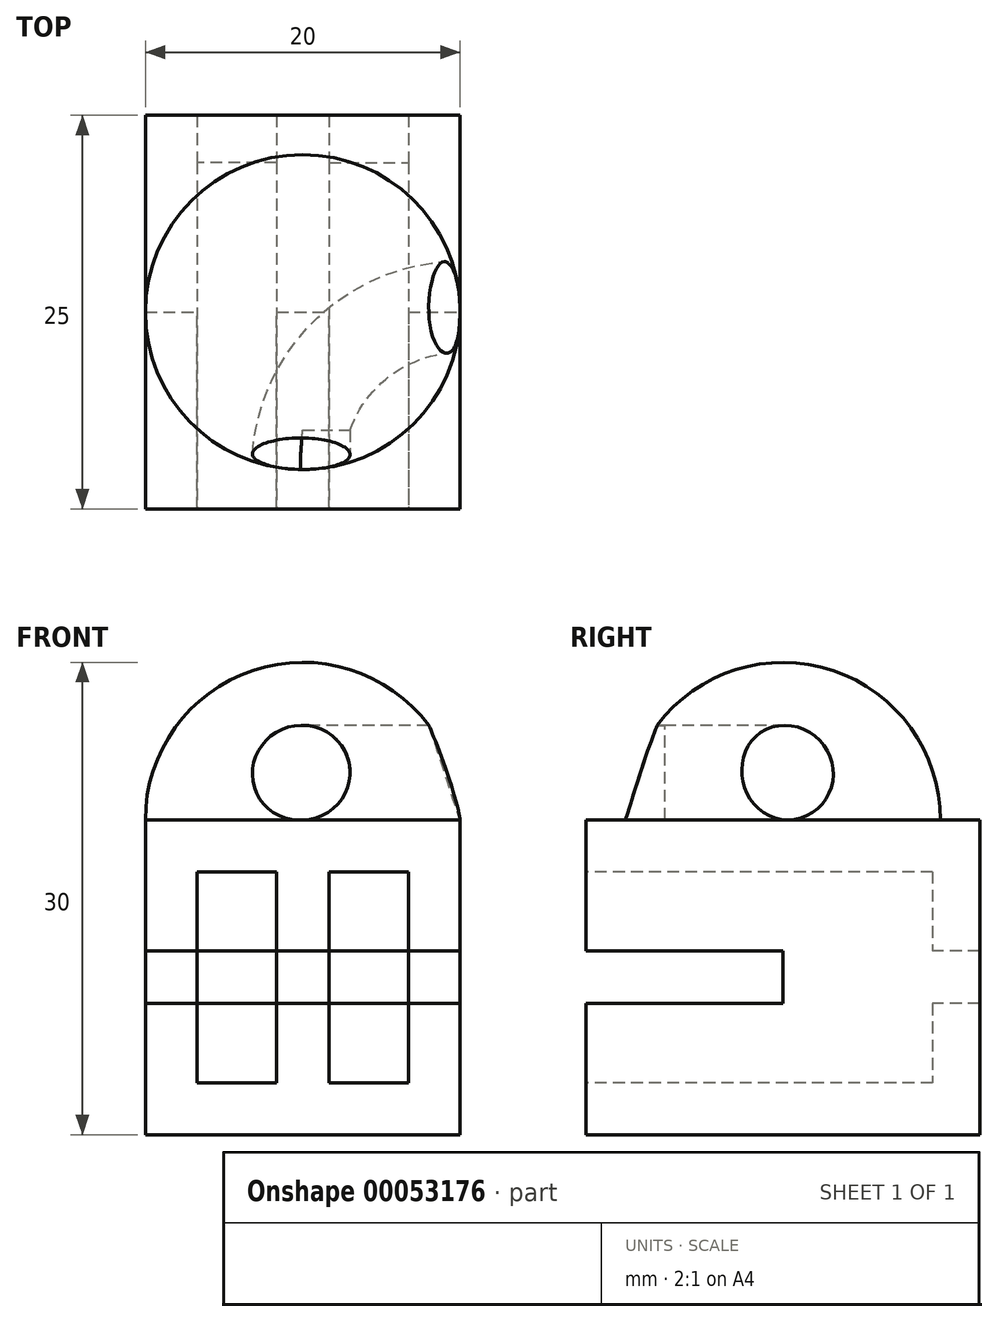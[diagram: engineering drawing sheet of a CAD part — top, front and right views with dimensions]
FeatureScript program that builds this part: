
annotation { "Feature Type Name" : "Feature", "Feature Type Description" : "" }
export const myFeature = defineFeature(function(context is Context, id is Id, definition is map)
    precondition{}
    {
        {
            var Q0;
            Q0=qCreatedBy(makeId("Front.planeOp"),FACE);
            var sketch = newSketch(context, id + "F0", { "sketchPlane" : qUnion([Q0])});
            skLineSegment(sketch, "E0.bottom", {"start": v(0, 0) * mm, "end": v(20, 0) * mm});
            skLineSegment(sketch, "E0.top", {"start": v(0, 20) * mm, "end": v(20, 20) * mm});
            skLineSegment(sketch, "E0.left", {"start": v(0, 0) * mm, "end": v(0, 20) * mm});
            skLineSegment(sketch, "E0.right", {"start": v(20, 0) * mm, "end": v(20, 20) * mm});
            skSolve(sketch);
        }
        {
            var Q0;
            Q0=makeQuery(id+"F0.imprint","IMPRINT",FACE,{"disambiguationData":[TD([[makeQuery(id+"F0.imprint","IMPRINT",EDGE,{"derivedFrom":sQuery(id+"F0.wireOp",EDGE,"E0.bottom")}),1.0]])]});
            extrude(context, id + "F1", {"entities" : qUnion([Q0]), "depth" : 25 * mm});
        }
        {
            var Q0;
            Q0=makeQuery(id+"F1.opExtrude","CAP_FACE",FACE,{"disambiguationData":[OSD([sQuery(id+"F0.wireOp",EDGE,"E0.bottom"),sQuery(id+"F0.wireOp",EDGE,"E0.top"),sQuery(id+"F0.wireOp",EDGE,"E0.left"),sQuery(id+"F0.wireOp",EDGE,"E0.right")])],"isStart":false});
            var sketch = newSketch(context, id + "F2", { "sketchPlane" : qUnion([Q0])});
            skLineSegment(sketch, "E1.rect.bottom", {"start": v(3.3, 16.7) * mm, "end": v(16.7, 16.7) * mm});
            skLineSegment(sketch, "E1.rect.top", {"start": v(3.3, 3.3) * mm, "end": v(16.7, 3.3) * mm});
            skLineSegment(sketch, "E1.rect.left", {"start": v(3.3, 16.7) * mm, "end": v(3.3, 3.3) * mm});
            skLineSegment(sketch, "E1.rect.right", {"start": v(16.7, 16.7) * mm, "end": v(16.7, 3.3) * mm});
            skPoint(sketch, "E1.rect.middle", {"position": v(10, 10) * mm});
            skPoint(sketch, "E1.rect.middle.positionSnap0", {"position": v(10, 20) * mm});
            skPoint(sketch, "E1.rect.middle.positionSnap1", {"position": v(0, 10) * mm});
            skPoint(sketch, "E1.rect.centerSnap0", {"position": v(10, 20) * mm});
            skPoint(sketch, "E1.rect.centerSnap1", {"position": v(0, 10) * mm});
            skSolve(sketch);
        }
        {
            var Q0;
            Q0=makeQuery(id+"F2.imprint","IMPRINT",FACE,{"disambiguationData":[TD([[makeQuery(id+"F2.imprint","IMPRINT",EDGE,{"derivedFrom":sQuery(id+"F2.wireOp",EDGE,"E1.rect.bottom")}),-1.0]])]});
            extrude(context, id + "F3", {"entities" : qUnion([Q0]), "operationType" : NewBodyOperationType.REMOVE, "oppositeDirection" : true, "depth" : 22 * mm});
        }
        {
            var Q0;
            Q0=makeQuery(id+"F1.opExtrude","CAP_FACE",FACE,{"disambiguationData":[OSD([sQuery(id+"F0.wireOp",EDGE,"E0.bottom"),sQuery(id+"F0.wireOp",EDGE,"E0.top"),sQuery(id+"F0.wireOp",EDGE,"E0.left"),sQuery(id+"F0.wireOp",EDGE,"E0.right")])],"isStart":false});
            var sketch = newSketch(context, id + "F4", { "sketchPlane" : qUnion([Q0])});
            skLineSegment(sketch, "E2", {"start": v(11.67, 16.7) * mm, "end": v(11.67, 3.3) * mm});
            skLineSegment(sketch, "E3", {"start": v(8.33, 3.3) * mm, "end": v(8.33, 16.7) * mm});
            skSolve(sketch);
        }
        {
            var Q0;
            {var subQ0=sQuery(id+"F4.wireOp",EDGE,"E2");Q0=makeQuery(id+"F4.imprint","IMPRINT",FACE,{"disambiguationData":[TD([[makeQuery(id+"F4.imprint","IMPRINT",EDGE,{"derivedFrom":subQ0}),-1.0]])]});}
            extrude(context, id + "F5", {"entities" : qUnion([Q0]), "operationType" : NewBodyOperationType.ADD, "oppositeDirection" : true, "depth" : 25 * mm});
        }
        {
            var Q0;
            Q0=makeQuery(id+"F1.opExtrude","SWEPT_FACE",FACE,{"disambiguationData":[OSD([sQuery(id+"F0.wireOp",EDGE,"E0.right")])]});
            var sketch = newSketch(context, id + "F6", { "sketchPlane" : qUnion([Q0])});
            skLineSegment(sketch, "E4", {"start": v(-25, 10) * mm, "end": v(-12.5, 10) * mm});
            skLineSegment(sketch, "E5", {"start": v(-12.5, 11.67) * mm, "end": v(-25, 11.67) * mm});
            skLineSegment(sketch, "E6", {"start": v(-25, 8.33) * mm, "end": v(-12.5, 8.33) * mm});
            skLineSegment(sketch, "E7", {"start": v(-12.5, 11.67) * mm, "end": v(-12.5, 8.33) * mm});
            skSolve(sketch);
        }
        {
            var Q0;
            {var subQ0=sQuery(id+"F6.wireOp",EDGE,"E4");Q0=makeQuery(id+"F6.imprint","IMPRINT",FACE,{"disambiguationData":[TD([[makeQuery(id+"F6.imprint","IMPRINT",EDGE,{"derivedFrom":subQ0}),1.0]])]});}
            var Q1;
            {var subQ0=sQuery(id+"F6.wireOp",EDGE,"E4");Q1=makeQuery(id+"F6.imprint","IMPRINT",FACE,{"disambiguationData":[TD([[makeQuery(id+"F6.imprint","IMPRINT",EDGE,{"derivedFrom":subQ0}),-1.0]])]});}
            extrude(context, id + "F7", {"entities" : qUnion([Q0, Q1]), "operationType" : NewBodyOperationType.REMOVE, "oppositeDirection" : true, "depth" : 25 * mm});
        }
        {
            var Q0;
            Q0=makeQuery(id+"F1.opExtrude","SWEPT_FACE",FACE,{"disambiguationData":[OSD([sQuery(id+"F0.wireOp",EDGE,"E0.top")])]});
            var sketch = newSketch(context, id + "F8", { "sketchPlane" : qUnion([Q0])});
            skLineSegment(sketch, "E8", {"start": v(0, -12.5) * mm, "end": v(10, -12.5) * mm});
            skPoint(sketch, "E8.endSnap0", {"position": v(10, 0) * mm});
            skCircle(sketch, "E9", {"center": v(10, -12.5) * mm, "radius": 10 * mm});
            skLineSegment(sketch, "E10", {"start": v(10, -12.5) * mm, "end": v(10, -2.5) * mm});
            skLineSegment(sketch, "E11", {"start": v(10, -12.5) * mm, "end": v(10, -22.5) * mm});
            skLineSegment(sketch, "E12", {"start": v(10, -22.5) * mm, "end": v(20, -22.5) * mm});
            skSolve(sketch);
        }
        {
            var Q0;
            {var subQ0=sQuery(id+"F8.wireOp",EDGE,"E10");Q0=makeQuery(id+"F8.imprint","IMPRINT",FACE,{"disambiguationData":[TD([[makeQuery(id+"F8.imprint","IMPRINT",EDGE,{"derivedFrom":subQ0}),-1.0]])]});}
            var Q1;
            Q1=sQuery(id+"F8.wireOp",EDGE,"E10");
            revolve(context, id + "F9", {"operationType" : NewBodyOperationType.ADD, "entities" : qUnion([Q0]), "axis" : qUnion([Q1]), "revolveType" : RevolveType.ONE_DIRECTION, "oppositeDirection" : true, "angle" : 180 * degree});
        }
        {
            var Q0;
            Q0=makeQuery(id+"F1.opExtrude","SWEPT_FACE",FACE,{"disambiguationData":[OSD([sQuery(id+"F0.wireOp",EDGE,"E0.right")])]});
            var sketch = newSketch(context, id + "F10", { "sketchPlane" : qUnion([Q0])});
            skLineSegment(sketch, "E13", {"start": v(-22.5, 20) * mm, "end": v(-22.5, 26) * mm});
            skSolve(sketch);
        }
        {
            var Q0;
            Q0=sQuery(id+"F8.wireOp",EDGE,"E12");
            var Q1;
            Q1=sQuery(id+"F10.wireOp",EDGE,"E13");
            cPlane(context, id + "F11", {"entities" : qUnion([Q0, Q1]), "cplaneType" : CPlaneType.LINE_ANGLE, "offset" : 150 * mm, "angle" : 0 * degree, "width" : 150 * mm, "height" : 150 * mm});
        }
        {
            var Q0;
            {var subQ0=sQuery(id+"F2.wireOp",EDGE,"E1.rect.bottom");var subQ1=sQuery(id+"F0.wireOp",EDGE,"E0.right");var subQ2=sQuery(id+"F0.wireOp",EDGE,"E0.left");var subQ3=sQuery(id+"F0.wireOp",EDGE,"E0.top");var subQ4=sQuery(id+"F4.wireOp",EDGE,"E2");var subQ5=sQuery(id+"F4.wireOp",EDGE,"E3");Q0=makeQuery(id+"F7.boolean.opBoolean","SPLIT",FACE,{"disambiguationData":[TD([makeQuery(id+"F1.opExtrude","SWEPT_FACE",FACE,{"disambiguationData":[OSD([subQ3])]})])],"derivedFrom":makeQuery(id+"F5.boolean.opBoolean","MERGE",FACE,{"derivedFrom":[makeQuery(id+"F1.opExtrude","CAP_FACE",FACE,{"disambiguationData":[OSD([sQuery(id+"F0.wireOp",EDGE,"E0.bottom"),subQ3,subQ2,subQ1])],"isStart":false}),makeQuery(id+"F5.opExtrude","CAP_FACE",FACE,{"disambiguationData":[OSD([subQ0,sQuery(id+"F2.wireOp",EDGE,"E1.rect.top"),subQ4,subQ5])],"isStart":true})]})});}
            var sketch = newSketch(context, id + "F12", { "sketchPlane" : qUnion([Q0])});
            skLineSegment(sketch, "E14", {"start": v(10, 20) * mm, "end": v(10, 26) * mm});
            skCircle(sketch, "E15", {"center": v(10, 23) * mm, "radius": 3 * mm});
            skSolve(sketch);
        }
        {
            var Q0;
            {var subQ0=sQuery(id+"F12.wireOp",EDGE,"E14");Q0=makeQuery(id+"F12.imprint","IMPRINT",FACE,{"disambiguationData":[TD([[makeQuery(id+"F12.imprint","IMPRINT",EDGE,{"derivedFrom":subQ0}),1.0]])]});}
            var Q1;
            {var subQ0=sQuery(id+"F12.wireOp",EDGE,"E14");Q1=makeQuery(id+"F12.imprint","IMPRINT",FACE,{"disambiguationData":[TD([[makeQuery(id+"F12.imprint","IMPRINT",EDGE,{"derivedFrom":subQ0}),-1.0]])]});}
            extrude(context, id + "F13", {"entities" : qUnion([Q0, Q1]), "oppositeDirection" : true, "depth" : 5 * mm});
        }
        {
            var Q0;
            Q0=qCreatedBy(id+"F11.planeOp",FACE);
            var sketch = newSketch(context, id + "F14", { "sketchPlane" : qUnion([Q0])});
            skLineSegment(sketch, "E16", {"start": v(0, 0) * mm, "end": v(0, 20) * mm});
            skLineSegment(sketch, "E17", {"start": v(0, 20) * mm, "end": v(20, 20) * mm});
            skLineSegment(sketch, "E18", {"start": v(20, 20) * mm, "end": v(20, 26) * mm});
            skSolve(sketch);
        }
        {
            var Q0;
            Q0=makeQuery(id+"F13.opExtrude","CAP_FACE",FACE,{"disambiguationData":[OSD([sQuery(id+"F12.wireOp",EDGE,"E15")])],"isStart":false});
            var Q1;
            Q1=sQuery(id+"F14.wireOp",EDGE,"E18");
            revolve(context, id + "F15", {"operationType" : NewBodyOperationType.REMOVE, "entities" : qUnion([Q0]), "axis" : qUnion([Q1]), "revolveType" : RevolveType.FULL, "oppositeDirection" : true});
        }
        {
            var Q0;
            Q0 = qSketchRegion(id + "F12", true);
            extrude(context, id + "F16", {"entities" : qUnion([Q0]), "operationType" : NewBodyOperationType.REMOVE, "oppositeDirection" : true, "depth" : 5 * mm});
        }
        {
            var Q0;
            Q0=makeQuery(id+"F7.boolean.opBoolean","COPY",FACE,{"disambiguationData":[TD([makeQuery(id+"F5.opExtrude","SWEPT_FACE",FACE,{"disambiguationData":[OSD([sQuery(id+"F4.wireOp",EDGE,"E2")])]})])],"derivedFrom":makeQuery(id+"F7.opExtrude","SWEPT_FACE",FACE,{"disambiguationData":[OSD([sQuery(id+"F6.wireOp",EDGE,"E7")])]})});
            var sketch = newSketch(context, id + "F17", { "sketchPlane" : qUnion([Q0])});
            skLineSegment(sketch, "E19", {"start": v(11.67, 8.33) * mm, "end": v(16.7, 8.33) * mm});
            skLineSegment(sketch, "E20", {"start": v(16.7, 8.33) * mm, "end": v(16.7, 11.67) * mm});
            skLineSegment(sketch, "E21", {"start": v(16.7, 11.67) * mm, "end": v(11.67, 11.67) * mm});
            skLineSegment(sketch, "E22", {"start": v(8.33, 8.33) * mm, "end": v(3.3, 8.33) * mm});
            skLineSegment(sketch, "E23", {"start": v(3.3, 8.33) * mm, "end": v(3.3, 11.67) * mm});
            skLineSegment(sketch, "E24", {"start": v(3.3, 11.67) * mm, "end": v(8.33, 11.67) * mm});
            skSolve(sketch);
        }
        {
            var Q0;
            Q0=makeQuery(id+"F17.imprint","IMPRINT",FACE,{"disambiguationData":[TD([[makeQuery(id+"F17.imprint","IMPRINT",EDGE,{"derivedFrom":sQuery(id+"F17.wireOp",EDGE,"E22")}),-1.0]])]});
            var Q1;
            Q1=makeQuery(id+"F17.imprint","IMPRINT",FACE,{"disambiguationData":[TD([[makeQuery(id+"F17.imprint","IMPRINT",EDGE,{"derivedFrom":sQuery(id+"F17.wireOp",EDGE,"E19")}),1.0]])]});
            extrude(context, id + "F18", {"entities" : qUnion([Q0, Q1]), "operationType" : NewBodyOperationType.REMOVE, "oppositeDirection" : true, "depth" : 25 * mm});
        }
    });
